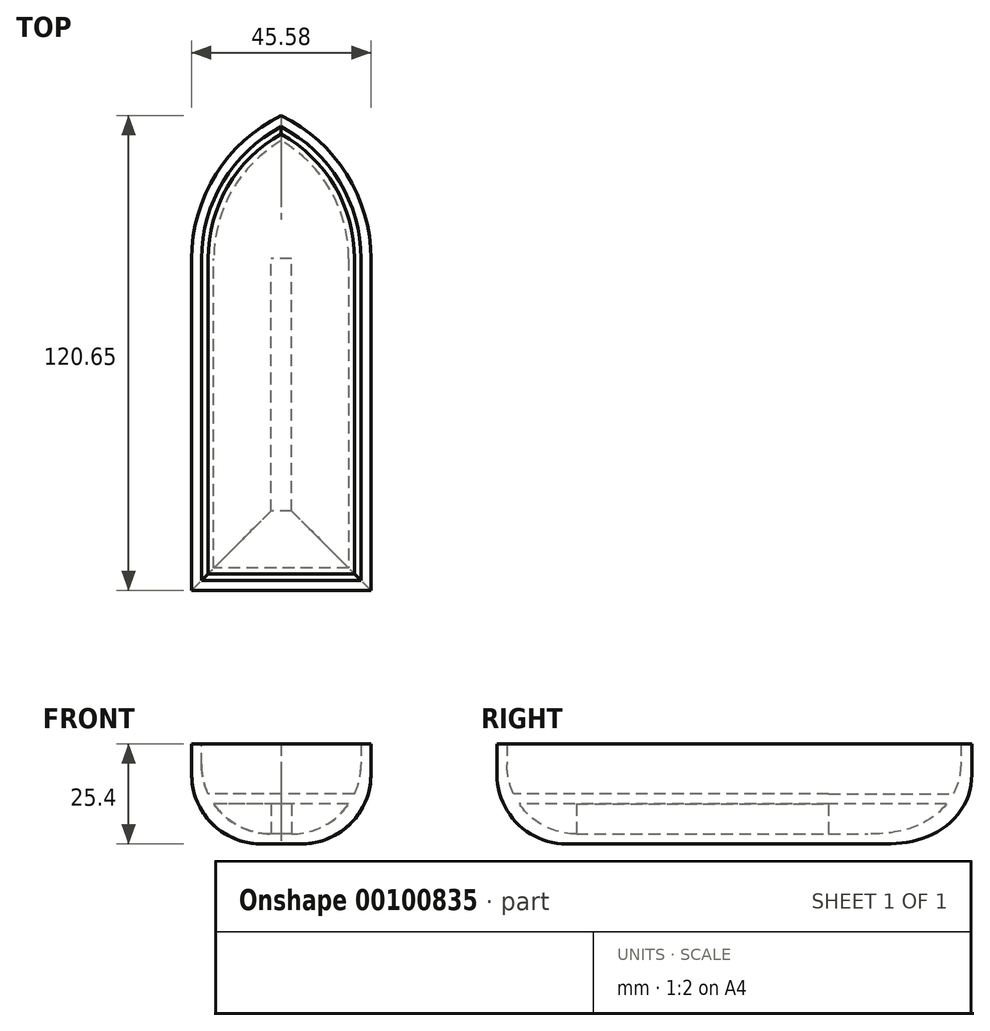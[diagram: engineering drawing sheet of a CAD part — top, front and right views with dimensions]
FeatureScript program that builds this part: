
annotation { "Feature Type Name" : "Feature", "Feature Type Description" : "" }
export const myFeature = defineFeature(function(context is Context, id is Id, definition is map)
    precondition{}
    {
        {
            var Q0;
            Q0=qCreatedBy(makeId("Top.planeOp"),FACE);
            var sketch = newSketch(context, id + "F0", { "sketchPlane" : qUnion([Q0])});
            skLineSegment(sketch, "E0.bottom", {"start": v(22.8, -56.53) * mm, "end": v(-22.8, -56.53) * mm});
            skLineSegment(sketch, "E0.top", {"start": v(22.8, 27.74) * mm, "end": v(-22.8, 27.74) * mm});
            skLineSegment(sketch, "E0.left", {"start": v(22.8, -56.53) * mm, "end": v(22.8, 27.74) * mm});
            skLineSegment(sketch, "E0.right", {"start": v(-22.8, -56.53) * mm, "end": v(-22.8, 27.74) * mm});
            skPoint(sketch, "E0.middle", {"position": v(0, -14.4) * mm});
            skArc(sketch, "E1", {"start": v(0, 64.12) * mm, "mid": v(-16.62, 49.2) * mm, "end": v(-22.8, 27.74) * mm});
            skArc(sketch, "E2", {"start": v(22.8, 27.74) * mm, "mid": v(16.62, 49.2) * mm, "end": v(0, 64.12) * mm});
            skSolve(sketch);
        }
        {
            var Q0;
            Q0=makeQuery(id+"F0.imprint","IMPRINT",FACE,{"disambiguationData":[TD([[makeQuery(id+"F0.imprint","IMPRINT",EDGE,{"derivedFrom":sQuery(id+"F0.wireOp",EDGE,"E0.top")}),-1.0]])]});
            var Q1;
            Q1=makeQuery(id+"F0.imprint","IMPRINT",FACE,{"disambiguationData":[TD([[makeQuery(id+"F0.imprint","IMPRINT",EDGE,{"derivedFrom":sQuery(id+"F0.wireOp",EDGE,"E0.bottom")}),-1.0]])]});
            extrude(context, id + "F1", {"entities" : qUnion([Q0, Q1]), "depth" : 25.4 * mm});
        }
        {
            var Q0;
            Q0=makeQuery(id+"F1.opExtrude","CAP_FACE",FACE,{"disambiguationData":[OSD([sQuery(id+"F0.wireOp",EDGE,"E0.bottom"),sQuery(id+"F0.wireOp",EDGE,"E0.left"),sQuery(id+"F0.wireOp",EDGE,"E0.right"),sQuery(id+"F0.wireOp",EDGE,"E1"),sQuery(id+"F0.wireOp",EDGE,"E2")])],"isStart":false});
            shell(context, id + "F2", {"entities" : qUnion([Q0]), "thickness" : 2.54 * mm});
        }
        {
            var Q0;
            Q0=makeQuery(id+"F1.opExtrude","CAP_EDGE",EDGE,{"disambiguationData":[OSD([sQuery(id+"F0.wireOp",EDGE,"E0.right")])],"isStart":true});
            var Q1;
            Q1=makeQuery(id+"F1.opExtrude","CAP_EDGE",EDGE,{"disambiguationData":[OSD([sQuery(id+"F0.wireOp",EDGE,"E1")])],"isStart":true});
            var Q2;
            {var subQ0=sQuery(id+"F0.wireOp",EDGE,"E0.left");Q2=makeQuery(id+"F2.opShell","OFFSET_EDGE",EDGE,{"disambiguationData":[OSD([subQ0]),TDD([makeQuery(id+"F1.opExtrude","CAP_EDGE",EDGE,{"disambiguationData":[OSD([subQ0])],"isStart":true})])]});}
            var Q3;
            {var subQ0=sQuery(id+"F0.wireOp",EDGE,"E2");Q3=makeQuery(id+"F2.opShell","OFFSET_EDGE",EDGE,{"disambiguationData":[OSD([subQ0]),TDD([makeQuery(id+"F1.opExtrude","CAP_EDGE",EDGE,{"disambiguationData":[OSD([subQ0])],"isStart":true})])]});}
            var Q4;
            {var subQ0=sQuery(id+"F0.wireOp",EDGE,"E0.right");Q4=makeQuery(id+"F2.opShell","OFFSET_EDGE",EDGE,{"disambiguationData":[OSD([subQ0]),TDD([makeQuery(id+"F1.opExtrude","CAP_EDGE",EDGE,{"disambiguationData":[OSD([subQ0])],"isStart":true})])]});}
            var Q5;
            {var subQ0=sQuery(id+"F0.wireOp",EDGE,"E1");Q5=makeQuery(id+"F2.opShell","OFFSET_EDGE",EDGE,{"disambiguationData":[OSD([subQ0]),TDD([makeQuery(id+"F1.opExtrude","CAP_EDGE",EDGE,{"disambiguationData":[OSD([subQ0])],"isStart":true})])]});}
            var Q6;
            Q6=makeQuery(id+"F1.opExtrude","CAP_EDGE",EDGE,{"disambiguationData":[OSD([sQuery(id+"F0.wireOp",EDGE,"E0.bottom")])],"isStart":true});
            var Q7;
            {var subQ0=sQuery(id+"F0.wireOp",EDGE,"E0.bottom");Q7=makeQuery(id+"F2.opShell","OFFSET_EDGE",EDGE,{"disambiguationData":[OSD([subQ0]),TDD([makeQuery(id+"F1.opExtrude","CAP_EDGE",EDGE,{"disambiguationData":[OSD([subQ0])],"isStart":true})])]});}
            var Q8;
            Q8=makeQuery(id+"F1.opExtrude","CAP_EDGE",EDGE,{"disambiguationData":[OSD([sQuery(id+"F0.wireOp",EDGE,"E0.left")])],"isStart":true});
            var Q9;
            Q9=makeQuery(id+"F1.opExtrude","CAP_EDGE",EDGE,{"disambiguationData":[OSD([sQuery(id+"F0.wireOp",EDGE,"E2")])],"isStart":true});
            fillet(context, id + "F3", {"entities" : qUnion([Q0, Q1, Q2, Q3, Q4, Q5, Q6, Q7, Q8, Q9]), "radius" : 17.6 * mm, "tangentPropagation" : true, "allowEdgeOverflow" : false});
        }
        {
            var Q0;
            Q0=makeQuery(id+"F2.opShell","OFFSET_FACE",FACE,{"disambiguationData":[OSD([sQuery(id+"F0.wireOp",EDGE,"E0.bottom"),sQuery(id+"F0.wireOp",EDGE,"E0.left"),sQuery(id+"F0.wireOp",EDGE,"E0.right"),sQuery(id+"F0.wireOp",EDGE,"E1"),sQuery(id+"F0.wireOp",EDGE,"E2")])]});
            var sketch = newSketch(context, id + "F4", { "sketchPlane" : qUnion([Q0])});
            skLineSegment(sketch, "E3.bottom", {"start": v(2.64, -36.37) * mm, "end": v(-2.64, -36.37) * mm});
            skLineSegment(sketch, "E3.top", {"start": v(2.64, 27.74) * mm, "end": v(-2.64, 27.74) * mm});
            skLineSegment(sketch, "E3.left", {"start": v(2.64, -36.37) * mm, "end": v(2.64, 27.74) * mm});
            skLineSegment(sketch, "E3.right", {"start": v(-2.64, -36.37) * mm, "end": v(-2.64, 27.74) * mm});
            skSolve(sketch);
        }
        {
            var Q0;
            Q0 = qSketchRegion(id + "F4", true);
            extrude(context, id + "F5", {"entities" : qUnion([Q0]), "operationType" : NewBodyOperationType.ADD, "depth" : 7.62 * mm});
        }
        {
            var Q0;
            Q0=makeQuery(id+"F5.opExtrude","CAP_FACE",FACE,{"disambiguationData":[OSD([sQuery(id+"F4.wireOp",EDGE,"E3.bottom"),sQuery(id+"F4.wireOp",EDGE,"E3.top"),sQuery(id+"F4.wireOp",EDGE,"E3.left"),sQuery(id+"F4.wireOp",EDGE,"E3.right")])],"isStart":false});
            var sketch = newSketch(context, id + "F6", { "sketchPlane" : qUnion([Q0])});
            skLineSegment(sketch, "E4.bottom", {"start": v(-20.5, 27.74) * mm, "end": v(20.03, 27.74) * mm});
            skLineSegment(sketch, "E4.top", {"start": v(-20.5, -53.76) * mm, "end": v(20.03, -53.76) * mm});
            skLineSegment(sketch, "E4.left", {"start": v(-20.5, 27.74) * mm, "end": v(-20.5, -53.76) * mm});
            skLineSegment(sketch, "E4.right", {"start": v(20.03, 27.74) * mm, "end": v(20.03, -53.76) * mm});
            skArc(sketch, "E5", {"start": v(0, 61.13) * mm, "mid": v(-14.96, 47.33) * mm, "end": v(-20.5, 27.74) * mm});
            skArc(sketch, "E6", {"start": v(20.03, 27.74) * mm, "mid": v(14.64, 47.21) * mm, "end": v(0, 61.13) * mm});
            skSolve(sketch);
        }
        {
            var Q0;
            Q0 = qSketchRegion(id + "F6", true);
            extrude(context, id + "F7", {"entities" : qUnion([Q0]), "operationType" : NewBodyOperationType.ADD, "depth" : 2.54 * mm});
        }
    });
